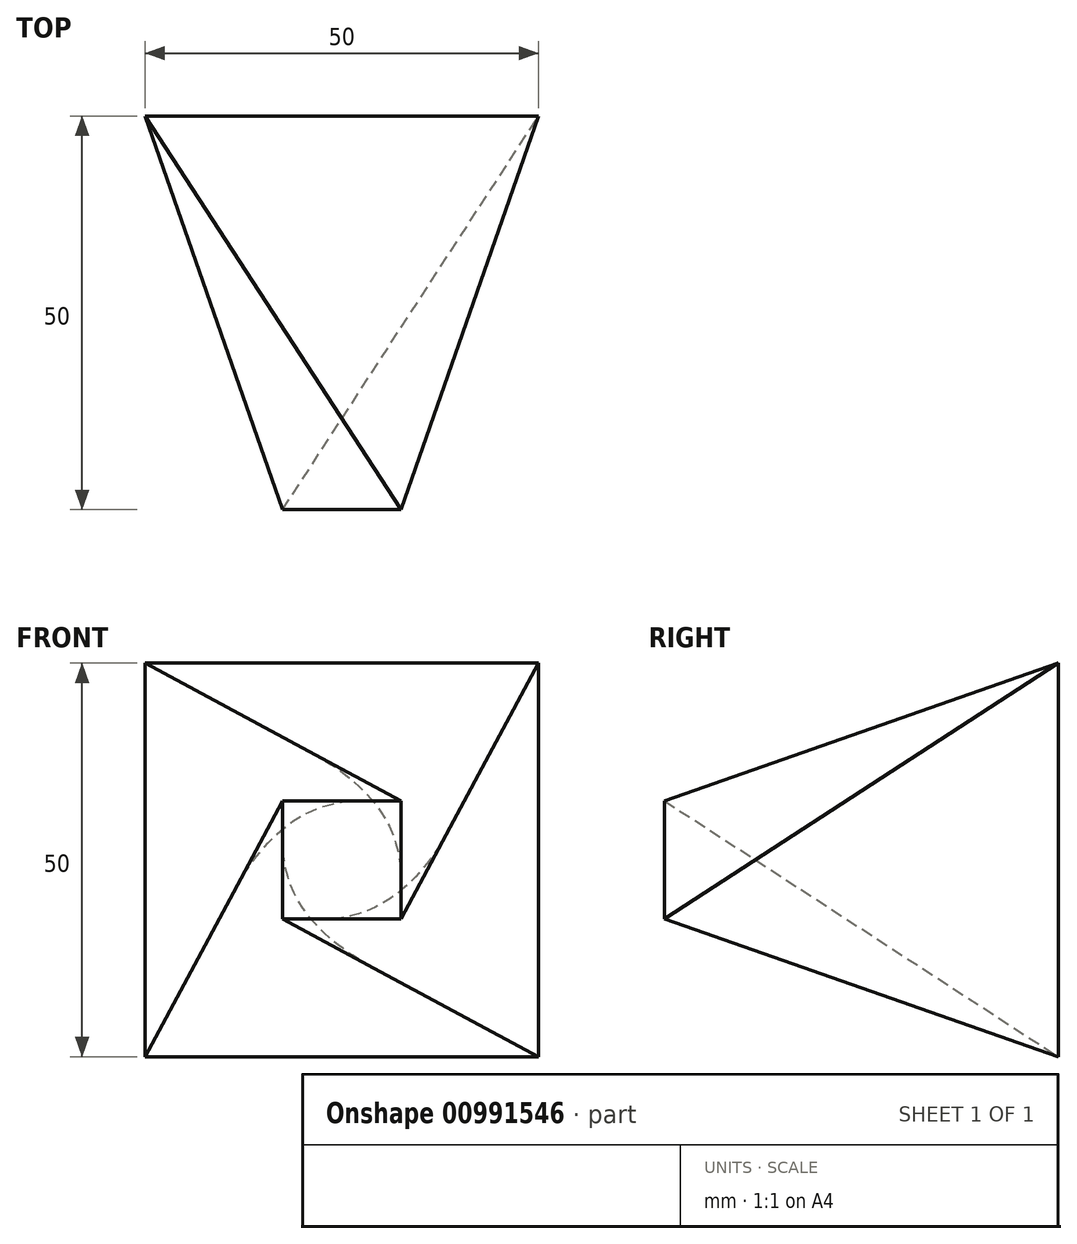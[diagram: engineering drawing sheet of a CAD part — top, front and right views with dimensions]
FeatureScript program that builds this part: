
annotation { "Feature Type Name" : "Feature", "Feature Type Description" : "" }
export const myFeature = defineFeature(function(context is Context, id is Id, definition is map)
    precondition{}
    {
        {
            var Q0;
            Q0=qCreatedBy(makeId("Front.planeOp"),FACE);
            var sketch = newSketch(context, id + "F0", { "sketchPlane" : qUnion([Q0])});
            skLineSegment(sketch, "E0.bottom", {"start": v(7.5, 7.5) * mm, "end": v(-7.5, 7.5) * mm});
            skLineSegment(sketch, "E0.top", {"start": v(7.5, -7.5) * mm, "end": v(-7.5, -7.5) * mm});
            skLineSegment(sketch, "E0.left", {"start": v(7.5, 7.5) * mm, "end": v(7.5, -7.5) * mm});
            skLineSegment(sketch, "E0.right", {"start": v(-7.5, 7.5) * mm, "end": v(-7.5, -7.5) * mm});
            skPoint(sketch, "E0.middle", {"position": v(0, 0) * mm});
            skSolve(sketch);
        }
        {
            var Q0;
            Q0=qCreatedBy(makeId("Front.planeOp"),FACE);
            cPlane(context, id + "F1", {"entities" : qUnion([Q0]), "cplaneType" : CPlaneType.OFFSET, "offset" : 50 * mm, "oppositeDirection" : true, "width" : 150 * mm, "height" : 150 * mm});
        }
        {
            var Q0;
            Q0=qCreatedBy(id+"F1.planeOp",FACE);
            var sketch = newSketch(context, id + "F2", { "sketchPlane" : qUnion([Q0])});
            skLineSegment(sketch, "E1.bottom", {"start": v(25, 25) * mm, "end": v(-25, 25) * mm});
            skLineSegment(sketch, "E1.top", {"start": v(25, -25) * mm, "end": v(-25, -25) * mm});
            skLineSegment(sketch, "E1.left", {"start": v(25, 25) * mm, "end": v(25, -25) * mm});
            skLineSegment(sketch, "E1.right", {"start": v(-25, 25) * mm, "end": v(-25, -25) * mm});
            skPoint(sketch, "E1.middle", {"position": v(0, 0) * mm});
            skSolve(sketch);
        }
        {
            var Q0;
            Q0=makeQuery(id+"F0.imprint","IMPRINT",FACE,{"disambiguationData":[TD([[makeQuery(id+"F0.imprint","IMPRINT",EDGE,{"derivedFrom":sQuery(id+"F0.wireOp",EDGE,"E0.bottom")}),1.0]])]});
            var Q1;
            Q1=makeQuery(id+"F2.imprint","IMPRINT",FACE,{"disambiguationData":[TD([[makeQuery(id+"F2.imprint","IMPRINT",EDGE,{"derivedFrom":sQuery(id+"F2.wireOp",EDGE,"E1.bottom")}),1.0]])]});
            var Q2;
            Q2=sQuery(id+"F0.wireOp",VERTEX,"E0.bottom.end");
            var Q3;
            Q3=sQuery(id+"F2.wireOp",VERTEX,"E1.top.end");
            loft(context, id + "F3", {"sheetProfilesArray" : [{ "sheetProfileEntities" : qUnion([Q0]) }, { "sheetProfileEntities" : qUnion([Q1]) }], "matchConnections" : true, "connections" : [{ "connectionEntities" : qUnion([Q2, Q3]), "connectionEdgeQueries" : qUnion([]), "connectionEdgeParameters" : [] }]});
        }
    });
